# Revit family: Kälteschelle ALU-PU 80 -s-, DS 20, M 8-M10, Ø 17,2- 57
name_source: partatom
category: HLS-Bauteile
revit_build: Autodesk Revit 2017 (Build: 20190507_1515(x64)
units: mm (PartAtom-declared; Revit-internal decimal feet)

## family parameters
Arbeitsebenenbasiert = Ja
Beim Laden mit Abzugskörper schneiden = Nein
Bemaßung runder Anschluss = Durchmesser verwenden
Gemeinsam genutzt = Ja
Immer vertikal = Nein
Raumberechnungspunkt = Nein
Teiletyp = Normal

## types (8) — shared parameters
A = 38 mm  [stored 0.124672 ft]
Anschluss = M8/M10
Baustoffklasse = B2
DS = 20 mm  [stored 0.0656168 ft]
DVS = 5 mm  [stored 0.0164042 ft]
Dichte Kern = 80 kg/m³
Dichte Mantel = 2.700 kg/m³
Dicke Mantel = 0,08 mm
Dämmkörper = ALU/PU
Dämmstärke = 20 mm  [stored 0.0656168 ft]
Fabrikat = MEFA
Firma = MEFA Befestigungs- und Montagesysteme GmbH
H1 = 2 mm  [stored 0.00656168 ft]
HGA = 16 mm  [stored 0.0524934 ft]
Kurztext1 = Kälteschelle RG80s ALU/PU
MD = 2 mm  [stored 0.00656168 ft]
Material = Stahl
Material Mantel = Alufolie
Materialname = DD11
Mengeneinheit = St
Oberflaeche = galvanisch verzinkt
Rohrschellentyp = Trabant
Vorgabe-Ansicht = 1219 mm
Wasserdampfdiffusionswiderstand = 18750 µ
Wärmeleitfähigkeit = 0.025 W/mK
max. Temperaturbeständigkeit = 120 °C
mittl. Nenndruckfestigkeit Kern = 0,5 N/mm²
stat. Belastung Kern = 0,1 N/mm²
vpe = 1 St

## per-type parameters (varying)
| type | Anschlußhöhe | Artikelnummer | B | Breite | D | D0 | DF1 | DF2 | EAN | Gewicht | Gewicht pro Bauteil | H | H2 | Kurztext2 | L | MB | R | RM | Rohraußendurchmesser Kupfer | Rohraußendurchmesser Stahl | S | Schalenlänge | max. zul. Last |
| Kälteschelle ALU-PU 80 -s-, DS 20, M8/M10, Ø 17,2 | 38 mm | 70401848 | 98 mm | 104 mm | 18 mm  [stored 0.0590551 ft] | 58 mm  [stored 0.190289 ft] | 18 mm  [stored 0.0590551 ft] | 19 mm  [stored 0.062336 ft] | 4250928441232 | 0.09 kg | 0.09 kg | 77 mm  [stored 0.252625 ft] | 3 mm  [stored 0.00984252 ft] | 17,2 mm Iso 20 x 40 mm M8/M10 | 40 mm  [stored 0.131234 ft] | 20 mm  [stored 0.0656168 ft] | 29 mm  [stored 0.0951444 ft] | 31 mm  [stored 0.101706 ft] | 18 mm | 17,2 mm | 80 mm  [stored 0.262467 ft] | 40 mm | 0.10 kN |
| Kälteschelle ALU-PU 80 -s-, DS 20, M8/M10, Ø 21,3 | 40 mm | 70402248 | 104 mm | 111 mm | 22 mm  [stored 0.0721785 ft] | 62 mm  [stored 0.203412 ft] | 19 mm  [stored 0.062336 ft] | 20 mm  [stored 0.0656168 ft] | 4250928441249 | 0.10 kg | 0.10 kg | 81 mm  [stored 0.265748 ft] | 3 mm  [stored 0.00984252 ft] | 21,3 mm Iso 20 x 40 mm M8/M10 | 40 mm  [stored 0.131234 ft] | 20 mm  [stored 0.0656168 ft] | 31 mm  [stored 0.101706 ft] | 33 mm | 22 mm | 21,3 mm | 85 mm | 40 mm | 0.10 kN |
| Kälteschelle ALU-PU 80 -s-, DS 20, M8/M10, Ø 26,9 | 40 mm | 70402848 | 111 mm | 119 mm | 28 mm  [stored 0.0918635 ft] | 68 mm | 20 mm  [stored 0.0656168 ft] | 20 mm  [stored 0.0656168 ft] | 4250928441256 | 0.11 kg | 0.11 kg | 87 mm | 3 mm  [stored 0.00984252 ft] | 26,9 mm Iso 20 x 40 mm M8/M10 | 40 mm  [stored 0.131234 ft] | 20 mm  [stored 0.0656168 ft] | 34 mm | 36 mm | 28 mm | 26,9 mm | 91 mm | 40 mm | 0.20 kN |
| Kälteschelle ALU-PU 80 -s-, DS 20, M8/M10, Ø 33,7 | 39 mm | 70403449 | 113 mm | 113 mm | 35 mm  [stored 0.114829 ft] | 75 mm | 17 mm  [stored 0.0557743 ft] | 17 mm  [stored 0.0557743 ft] | 4250928441263 | 0.13 kg | 0.13 kg | 95 mm | 4 mm  [stored 0.0131234 ft] | 33,7 mm Iso 20 x 40 mm M8/M10 | 40 mm  [stored 0.131234 ft] | 20 mm  [stored 0.0656168 ft] | 38 mm  [stored 0.124672 ft] | 40 mm  [stored 0.131234 ft] | 35 mm | 33,7 mm | 96 mm | 40 mm | 0.20 kN |
| Kälteschelle ALU-PU 80 -s-, DS 20, M8/M10, Ø 42,4 | 39 mm | 70404248 | 127 mm | 128 mm | 42 mm | 82 mm | 21 mm  [stored 0.0688976 ft] | 21 mm  [stored 0.0688976 ft] | 4250928441270 | 0.14 kg | 0.14 kg | 101 mm | 3 mm  [stored 0.00984252 ft] | 42,4 mm Iso 20 x 40 mm M8/M10 | 40 mm  [stored 0.131234 ft] | 25 mm  [stored 0.082021 ft] | 41 mm | 43 mm | 42 mm | 42,4 mm | 106 mm | 40 mm | 0.20 kN |
| Kälteschelle ALU-PU 80 -s-, DS 20, M8/M10, Ø 48,3 | 39 mm | 70504849 | 131 mm | 124 mm | 48 mm  [stored 0.15748 ft] | 88 mm | 20 mm  [stored 0.0656168 ft] | 19 mm  [stored 0.062336 ft] | 4250928441287 | 0.15 kg | 0.15 kg | 108 mm | 4 mm  [stored 0.0131234 ft] | 48,3 mm Iso 20 x 50 mm M8/M10 | 50 mm  [stored 0.164042 ft] | 20 mm  [stored 0.0656168 ft] | 44 mm | 46 mm  [stored 0.150919 ft] |  | 48,3 mm | 111 mm | 50 mm | 0.30 kN |
| Kälteschelle ALU-PU 80 -s-, DS 20, M8/M10, Ø 54 | 43 mm | 70505448 | 134 mm | 141 mm | 54 mm  [stored 0.177165 ft] | 94 mm | 18 mm  [stored 0.0590551 ft] | 18 mm  [stored 0.0590551 ft] | 4250928441294 | 0.19 kg | 0.19 kg | 114 mm | 4 mm  [stored 0.0131234 ft] | 54 mm Iso 20 x 50 mm M8/M10 | 50 mm  [stored 0.164042 ft] | 25 mm  [stored 0.082021 ft] | 47 mm  [stored 0.154199 ft] | 49 mm  [stored 0.160761 ft] |  | 54 mm | 116 mm | 50 mm | 0.30 kN |
| Kälteschelle ALU-PU 80 -s-, DS 20, M8/M10, Ø 57 | 38 mm | 70505748 | 137 mm | 141 mm | 57 mm  [stored 0.187008 ft] | 97 mm | 18 mm  [stored 0.0590551 ft] | 18 mm  [stored 0.0590551 ft] | 4250928441300 | 0.19 kg | 0.19 kg | 117 mm | 4 mm  [stored 0.0131234 ft] | 57 mm Iso 20 x 50 mm M8/M10 | 50 mm  [stored 0.164042 ft] | 25 mm  [stored 0.082021 ft] | 49 mm  [stored 0.160761 ft] | 51 mm |  | 57 mm | 119 mm | 50 mm | 0.40 kN |

note: [stored X ft] marks values corroborated as IEEE doubles in the binary element streams (Revit-internal decimal feet)

## geometry (parser evidence)
native form markers: Sweep x2
no freeform markers — native parametric forms only
